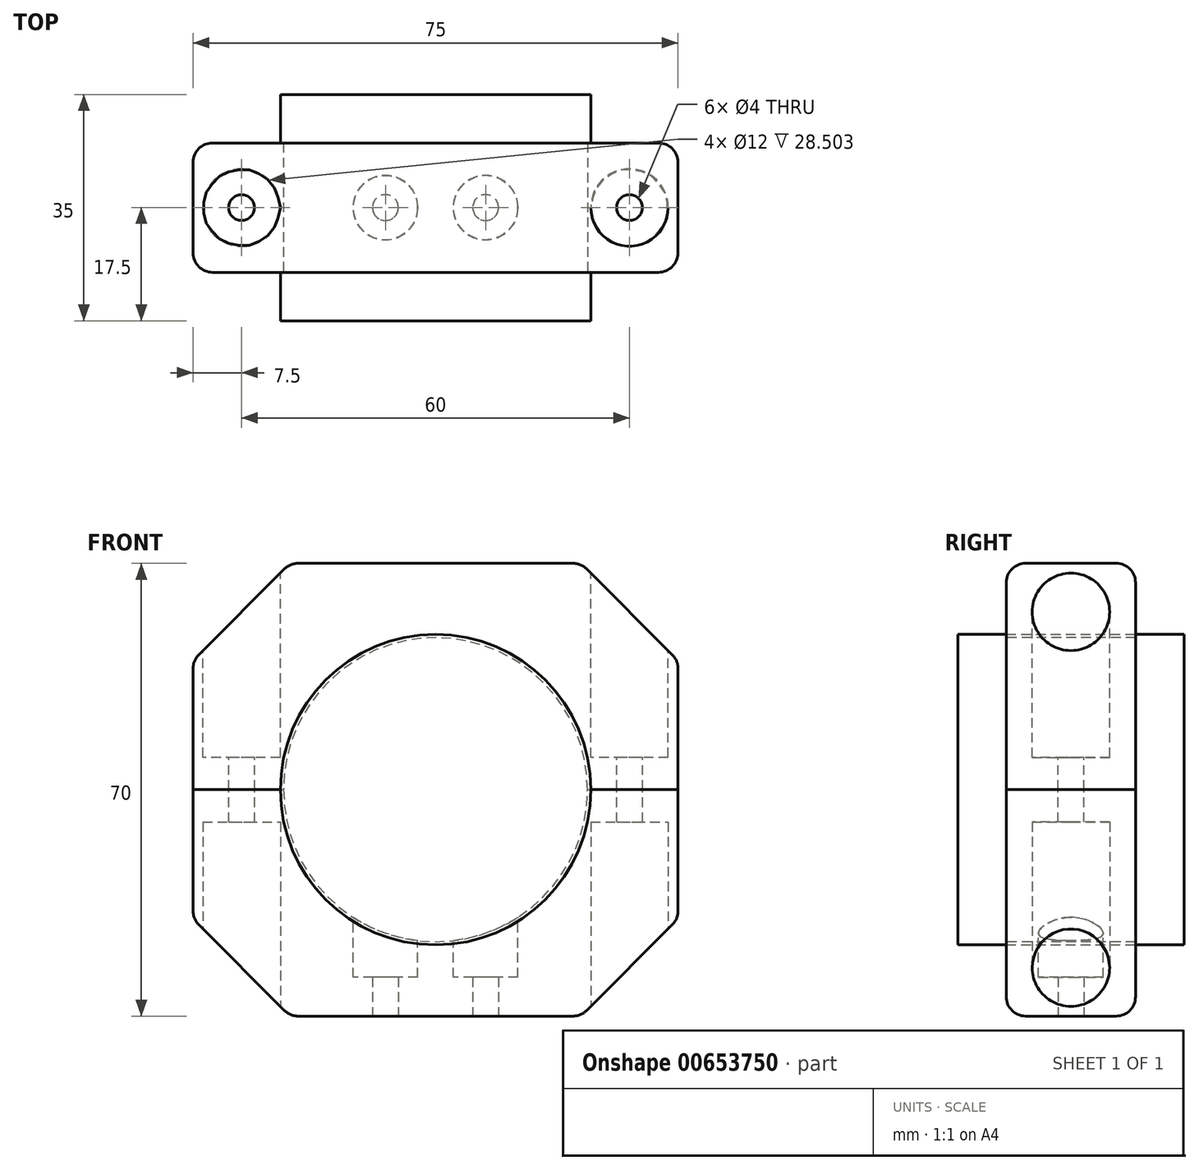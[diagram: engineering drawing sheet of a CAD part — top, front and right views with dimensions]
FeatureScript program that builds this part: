
annotation { "Feature Type Name" : "Feature", "Feature Type Description" : "" }
export const myFeature = defineFeature(function(context is Context, id is Id, definition is map)
    precondition{}
    {
        {
            var Q0;
            Q0=qCreatedBy(makeId("Top.planeOp"),FACE);
            var sketch = newSketch(context, id + "F0", { "sketchPlane" : qUnion([Q0])});
            skLineSegment(sketch, "E0.bottom", {"start": v(15, -10) * mm, "end": v(-15, -10) * mm});
            skLineSegment(sketch, "E0.top", {"start": v(15, 10) * mm, "end": v(-15, 10) * mm});
            skLineSegment(sketch, "E0.left", {"start": v(15, -10) * mm, "end": v(15, 10) * mm});
            skLineSegment(sketch, "E0.right", {"start": v(-15, -10) * mm, "end": v(-15, 10) * mm});
            skPoint(sketch, "E0.middle", {"position": v(0, 0) * mm});
            skLineSegment(sketch, "E1.bottom", {"start": v(37.5, -10) * mm, "end": v(-37.5, -10) * mm});
            skLineSegment(sketch, "E1.top", {"start": v(37.5, 10) * mm, "end": v(-37.5, 10) * mm});
            skLineSegment(sketch, "E1.left", {"start": v(37.5, -10) * mm, "end": v(37.5, 10) * mm});
            skLineSegment(sketch, "E1.right", {"start": v(-37.5, -10) * mm, "end": v(-37.5, 10) * mm});
            skSolve(sketch);
        }
        {
            var Q0;
            Q0 = qSketchRegion(id + "F0", true);
            extrude(context, id + "F1", {"entities" : qUnion([Q0]), "depth" : 35 * mm, "offsetDistance" : 25 * mm});
        }
        {
            var Q0;
            Q0=qCreatedBy(makeId("Front.planeOp"),FACE);
            var sketch = newSketch(context, id + "F2", { "sketchPlane" : qUnion([Q0])});
            skCircle(sketch, "E2", {"center": v(0, 35) * mm, "radius": 23.5 * mm});
            skSolve(sketch);
        }
        {
            var Q0;
            Q0 = qSketchRegion(id + "F2", true);
            var Q1;
            Q1=makeQuery(id+"F11.opExtrude","SWEPT_FACE",FACE,{"disambiguationData":[OSD([sQuery(id+"F10.wireOp",EDGE,"E9.bottom")])]});
            extrude(context, id + "F3", {"entities" : qUnion([Q0, Q1]), "operationType" : NewBodyOperationType.REMOVE, "endBound" : BoundingType.SYMMETRIC, "oppositeDirection" : true, "depth" : 50 * mm, "offsetDistance" : 25 * mm});
        }
        {
            var Q0;
            Q0=makeQuery(id+"F1.opExtrude","CAP_FACE",FACE,{"disambiguationData":[OSD([sQuery(id+"F0.wireOp",EDGE,"E1.bottom"),sQuery(id+"F0.wireOp",EDGE,"E1.top"),sQuery(id+"F0.wireOp",EDGE,"E1.left"),sQuery(id+"F0.wireOp",EDGE,"E1.right")])],"isStart":true});
            var sketch = newSketch(context, id + "F4", { "sketchPlane" : qUnion([Q0])});
            skCircle(sketch, "E3", {"center": v(7.75, 0) * mm, "radius": 2 * mm});
            skCircle(sketch, "E4.MirrorC", {"center": v(-7.75, 0) * mm, "radius": 2 * mm});
            skSolve(sketch);
        }
        {
            var Q0;
            Q0 = qSketchRegion(id + "F4", true);
            extrude(context, id + "F5", {"entities" : qUnion([Q0]), "operationType" : NewBodyOperationType.REMOVE, "oppositeDirection" : true, "depth" : 25 * mm, "offsetDistance" : 25 * mm});
        }
        {
            var Q0;
            {var subQ0=sQuery(id+"F0.wireOp",EDGE,"E1.bottom");var subQ1=sQuery(id+"F0.wireOp",EDGE,"E1.top");var subQ2=sQuery(id+"F0.wireOp",EDGE,"E1.left");Q0=makeQuery(id+"F3.boolean.opBoolean","SPLIT",FACE,{"disambiguationData":[TD([makeQuery(id+"F1.opExtrude","SWEPT_FACE",FACE,{"disambiguationData":[OSD([subQ2])]})])],"derivedFrom":makeQuery(id+"F1.opExtrude","CAP_FACE",FACE,{"disambiguationData":[OSD([subQ0,subQ1,subQ2,sQuery(id+"F0.wireOp",EDGE,"E1.right")])],"isStart":false})});}
            var sketch = newSketch(context, id + "F6", { "sketchPlane" : qUnion([Q0])});
            skCircle(sketch, "E5", {"center": v(7.75, 0) * mm, "radius": 5 * mm});
            skCircle(sketch, "E6.MirrorC", {"center": v(-7.75, 0) * mm, "radius": 5 * mm});
            skSolve(sketch);
        }
        {
            var Q0;
            Q0 = qSketchRegion(id + "F6", true);
            extrude(context, id + "F7", {"entities" : qUnion([Q0]), "operationType" : NewBodyOperationType.REMOVE, "oppositeDirection" : true, "depth" : 29 * mm, "offsetDistance" : 25 * mm});
        }
        {
            var Q0;
            {var subQ0=sQuery(id+"F0.wireOp",EDGE,"E1.bottom");var subQ1=sQuery(id+"F0.wireOp",EDGE,"E1.right");var subQ2=sQuery(id+"F0.wireOp",EDGE,"E1.top");Q0=makeQuery(id+"F3.boolean.opBoolean","SPLIT",FACE,{"disambiguationData":[TD([makeQuery(id+"F1.opExtrude","SWEPT_FACE",FACE,{"disambiguationData":[OSD([subQ1])]})])],"derivedFrom":makeQuery(id+"F1.opExtrude","CAP_FACE",FACE,{"disambiguationData":[OSD([subQ0,subQ2,sQuery(id+"F0.wireOp",EDGE,"E1.left"),subQ1])],"isStart":false})});}
            var sketch = newSketch(context, id + "F8", { "sketchPlane" : qUnion([Q0])});
            skCircle(sketch, "E7", {"center": v(30, 0) * mm, "radius": 2 * mm});
            skCircle(sketch, "E8.MirrorC", {"center": v(-30, 0) * mm, "radius": 2 * mm});
            skSolve(sketch);
        }
        {
            var Q0;
            Q0 = qSketchRegion(id + "F8", true);
            extrude(context, id + "F9", {"entities" : qUnion([Q0]), "operationType" : NewBodyOperationType.REMOVE, "endBound" : BoundingType.THROUGH_ALL, "oppositeDirection" : true, "depth" : 50 * mm, "offsetDistance" : 25 * mm, "hasSecondDirection" : true, "secondDirectionBound" : SecondDirectionBoundingType.THROUGH_ALL, "secondDirectionOppositeDirection" : false, "secondDirectionDepth" : 25 * mm});
        }
        {
            var Q0;
            {var subQ0=sQuery(id+"F0.wireOp",EDGE,"E1.bottom");var subQ1=sQuery(id+"F0.wireOp",EDGE,"E1.right");var subQ2=sQuery(id+"F0.wireOp",EDGE,"E1.top");Q0=makeQuery(id+"F3.boolean.opBoolean","SPLIT",FACE,{"disambiguationData":[TD([makeQuery(id+"F1.opExtrude","SWEPT_FACE",FACE,{"disambiguationData":[OSD([subQ1])]})])],"derivedFrom":makeQuery(id+"F1.opExtrude","CAP_FACE",FACE,{"disambiguationData":[OSD([subQ0,subQ2,sQuery(id+"F0.wireOp",EDGE,"E1.left"),subQ1])],"isStart":false})});}
            var sketch = newSketch(context, id + "F10", { "sketchPlane" : qUnion([Q0])});
            skLineSegment(sketch, "E9.bottom", {"start": v(-37.5, -10) * mm, "end": v(37.5, -10) * mm});
            skLineSegment(sketch, "E9.top", {"start": v(-37.5, 10) * mm, "end": v(37.5, 10) * mm});
            skLineSegment(sketch, "E9.left", {"start": v(-37.5, -10) * mm, "end": v(-37.5, 10) * mm});
            skLineSegment(sketch, "E9.right", {"start": v(37.5, -10) * mm, "end": v(37.5, 10) * mm});
            skSolve(sketch);
        }
        {
            var Q0;
            Q0 = qSketchRegion(id + "F10", true);
            extrude(context, id + "F11", {"entities" : qUnion([Q0]), "depth" : 35 * mm, "offsetDistance" : 25 * mm});
        }
        {
            var Q0;
            Q0=makeQuery(id+"F11.opExtrude","SWEPT_FACE",FACE,{"disambiguationData":[OSD([sQuery(id+"F10.wireOp",EDGE,"E9.bottom")])]});
            var sketch = newSketch(context, id + "F12", { "sketchPlane" : qUnion([Q0])});
            skCircle(sketch, "E10", {"center": v(0, 35) * mm, "radius": 23.5 * mm});
            skSolve(sketch);
        }
        {
            var Q0;
            Q0 = qSketchRegion(id + "F12", true);
            extrude(context, id + "F13", {"entities" : qUnion([Q0]), "operationType" : NewBodyOperationType.REMOVE, "endBound" : BoundingType.SYMMETRIC, "oppositeDirection" : true, "depth" : 50 * mm, "offsetDistance" : 25 * mm});
        }
        {
            var Q0;
            Q0=makeQuery(id+"F11.opExtrude","CAP_FACE",FACE,{"disambiguationData":[OSD([sQuery(id+"F10.wireOp",EDGE,"E9.bottom"),sQuery(id+"F10.wireOp",EDGE,"E9.top"),sQuery(id+"F10.wireOp",EDGE,"E9.left"),sQuery(id+"F10.wireOp",EDGE,"E9.right")])],"isStart":false});
            var sketch = newSketch(context, id + "F14", { "sketchPlane" : qUnion([Q0])});
            skCircle(sketch, "E11", {"center": v(30, 0) * mm, "radius": 2 * mm});
            skCircle(sketch, "E12.MirrorC", {"center": v(-30, 0) * mm, "radius": 2 * mm});
            skSolve(sketch);
        }
        {
            var Q0;
            Q0 = qSketchRegion(id + "F14", true);
            extrude(context, id + "F15", {"entities" : qUnion([Q0]), "operationType" : NewBodyOperationType.REMOVE, "oppositeDirection" : true, "depth" : 50 * mm, "offsetDistance" : 25 * mm});
        }
        {
            var Q0;
            Q0=makeQuery(id+"F11.opExtrude","CAP_FACE",FACE,{"disambiguationData":[OSD([sQuery(id+"F10.wireOp",EDGE,"E9.bottom"),sQuery(id+"F10.wireOp",EDGE,"E9.top"),sQuery(id+"F10.wireOp",EDGE,"E9.left"),sQuery(id+"F10.wireOp",EDGE,"E9.right")])],"isStart":false});
            var sketch = newSketch(context, id + "F16", { "sketchPlane" : qUnion([Q0])});
            skCircle(sketch, "E13", {"center": v(30, 0) * mm, "radius": 6 * mm});
            skCircle(sketch, "E14.MirrorC", {"center": v(-30, 0) * mm, "radius": 6 * mm});
            skSolve(sketch);
        }
        {
            var Q0;
            Q0 = qSketchRegion(id + "F16", true);
            extrude(context, id + "F17", {"entities" : qUnion([Q0]), "operationType" : NewBodyOperationType.REMOVE, "oppositeDirection" : true, "depth" : 30 * mm, "offsetDistance" : 25 * mm});
        }
        {
            var Q0;
            {var subQ0=sQuery(id+"F10.wireOp",EDGE,"E9.bottom");var subQ1=sQuery(id+"F10.wireOp",EDGE,"E9.right");Q0=makeQuery(id+"F17.boolean.opBoolean","SPLIT",EDGE,{"disambiguationData":[TD([makeQuery(id+"F11.opExtrude","SWEPT_FACE",FACE,{"disambiguationData":[OSD([subQ0])]})])],"derivedFrom":makeQuery(id+"F11.opExtrude","CAP_EDGE",EDGE,{"disambiguationData":[OSD([subQ1])],"isStart":false})});}
            var Q1;
            {var subQ0=sQuery(id+"F10.wireOp",EDGE,"E9.right");var subQ1=sQuery(id+"F10.wireOp",EDGE,"E9.top");Q1=makeQuery(id+"F17.boolean.opBoolean","SPLIT",EDGE,{"disambiguationData":[TD([makeQuery(id+"F11.opExtrude","SWEPT_FACE",FACE,{"disambiguationData":[OSD([subQ1])]})])],"derivedFrom":makeQuery(id+"F11.opExtrude","CAP_EDGE",EDGE,{"disambiguationData":[OSD([subQ0])],"isStart":false})});}
            var Q2;
            {var subQ0=sQuery(id+"F10.wireOp",EDGE,"E9.bottom");var subQ1=sQuery(id+"F10.wireOp",EDGE,"E9.left");Q2=makeQuery(id+"F17.boolean.opBoolean","SPLIT",EDGE,{"disambiguationData":[TD([makeQuery(id+"F11.opExtrude","SWEPT_FACE",FACE,{"disambiguationData":[OSD([subQ0])]})])],"derivedFrom":makeQuery(id+"F11.opExtrude","CAP_EDGE",EDGE,{"disambiguationData":[OSD([subQ1])],"isStart":false})});}
            var Q3;
            {var subQ0=sQuery(id+"F10.wireOp",EDGE,"E9.left");var subQ1=sQuery(id+"F10.wireOp",EDGE,"E9.top");Q3=makeQuery(id+"F17.boolean.opBoolean","SPLIT",EDGE,{"disambiguationData":[TD([makeQuery(id+"F11.opExtrude","SWEPT_FACE",FACE,{"disambiguationData":[OSD([subQ1])]})])],"derivedFrom":makeQuery(id+"F11.opExtrude","CAP_EDGE",EDGE,{"disambiguationData":[OSD([subQ0])],"isStart":false})});}
            chamfer(context, id + "F18", {"entities" : qUnion([Q0, Q1, Q2, Q3]), "width" : 15 * mm, "tangentPropagation" : true});
        }
        {
            var Q0;
            Q0=makeQuery(id+"F1.opExtrude","CAP_EDGE",EDGE,{"disambiguationData":[OSD([sQuery(id+"F0.wireOp",EDGE,"E1.left")])],"isStart":true});
            var Q1;
            Q1=makeQuery(id+"F1.opExtrude","CAP_EDGE",EDGE,{"disambiguationData":[OSD([sQuery(id+"F0.wireOp",EDGE,"E1.right")])],"isStart":true});
            chamfer(context, id + "F19", {"entities" : qUnion([Q0, Q1]), "width" : 15 * mm, "tangentPropagation" : true});
        }
        {
            var Q0;
            Q0=qCreatedBy(makeId("Front.planeOp"),FACE);
            var sketch = newSketch(context, id + "F20", { "sketchPlane" : qUnion([Q0])});
            skCircle(sketch, "E15", {"center": v(0, 35) * mm, "radius": 24 * mm});
            skSolve(sketch);
        }
        {
            var Q0;
            Q0 = qSketchRegion(id + "F20", true);
            extrude(context, id + "F21", {"entities" : qUnion([Q0]), "endBound" : BoundingType.SYMMETRIC, "depth" : 35 * mm, "offsetDistance" : 25 * mm});
        }
        {
            var Q0;
            {var subQ0=sQuery(id+"F10.wireOp",EDGE,"E9.right");var subQ1=sQuery(id+"F10.wireOp",EDGE,"E9.bottom");var subQ2=makeQuery(id+"F11.opExtrude","CAP_FACE",FACE,{"disambiguationData":[OSD([subQ1,sQuery(id+"F10.wireOp",EDGE,"E9.top"),sQuery(id+"F10.wireOp",EDGE,"E9.left"),subQ0])],"isStart":false});Q0=makeQuery(id+"F18.opChamfer","BLEND_EDGE",EDGE,{"blendedFrom":[makeQuery(id+"F17.boolean.opBoolean","SPLIT",EDGE,{"disambiguationData":[TD([makeQuery(id+"F11.opExtrude","SWEPT_FACE",FACE,{"disambiguationData":[OSD([subQ1])]})])],"derivedFrom":makeQuery(id+"F11.opExtrude","CAP_EDGE",EDGE,{"disambiguationData":[OSD([subQ0])],"isStart":false})}),subQ2],"blendedInto":[subQ2]});}
            var Q1;
            {var subQ0=sQuery(id+"F10.wireOp",EDGE,"E9.right");var subQ1=makeQuery(id+"F11.opExtrude","SWEPT_FACE",FACE,{"disambiguationData":[OSD([subQ0])]});var subQ2=sQuery(id+"F10.wireOp",EDGE,"E9.bottom");Q1=makeQuery(id+"F18.opChamfer","BLEND_EDGE",EDGE,{"disambiguationData":[OD(0.0)],"blendedFrom":[makeQuery(id+"F17.boolean.opBoolean","SPLIT",EDGE,{"disambiguationData":[TD([makeQuery(id+"F11.opExtrude","SWEPT_FACE",FACE,{"disambiguationData":[OSD([subQ2])]})])],"derivedFrom":makeQuery(id+"F11.opExtrude","CAP_EDGE",EDGE,{"disambiguationData":[OSD([subQ0])],"isStart":false})}),subQ1],"blendedInto":[subQ1]});}
            var Q2;
            {var subQ0=sQuery(id+"F10.wireOp",EDGE,"E9.right");var subQ1=makeQuery(id+"F11.opExtrude","SWEPT_FACE",FACE,{"disambiguationData":[OSD([subQ0])]});var subQ2=sQuery(id+"F10.wireOp",EDGE,"E9.bottom");Q2=makeQuery(id+"F18.opChamfer","BLEND_EDGE",EDGE,{"disambiguationData":[OD(1.0)],"blendedFrom":[makeQuery(id+"F17.boolean.opBoolean","SPLIT",EDGE,{"disambiguationData":[TD([makeQuery(id+"F11.opExtrude","SWEPT_FACE",FACE,{"disambiguationData":[OSD([subQ2])]})])],"derivedFrom":makeQuery(id+"F11.opExtrude","CAP_EDGE",EDGE,{"disambiguationData":[OSD([subQ0])],"isStart":false})}),subQ1],"blendedInto":[subQ1]});}
            var Q3;
            Q3=makeQuery(id+"F11.opExtrude","CAP_EDGE",EDGE,{"disambiguationData":[OSD([sQuery(id+"F10.wireOp",EDGE,"E9.bottom")])],"isStart":false});
            var Q4;
            {var subQ0=sQuery(id+"F10.wireOp",EDGE,"E9.bottom");var subQ1=makeQuery(id+"F11.opExtrude","SWEPT_FACE",FACE,{"disambiguationData":[OSD([subQ0])]});var subQ2=sQuery(id+"F10.wireOp",EDGE,"E9.right");Q4=makeQuery(id+"F18.opChamfer","BLEND_EDGE",EDGE,{"blendedFrom":[makeQuery(id+"F17.boolean.opBoolean","SPLIT",EDGE,{"disambiguationData":[TD([subQ1])],"derivedFrom":makeQuery(id+"F11.opExtrude","CAP_EDGE",EDGE,{"disambiguationData":[OSD([subQ2])],"isStart":false})}),subQ1],"blendedInto":[subQ1]});}
            var Q5;
            Q5=makeQuery(id+"F11.opExtrude","SWEPT_EDGE",EDGE,{"disambiguationData":[OSD([sQuery(id+"F10.wireOp",EDGE,"E9.bottom"),sQuery(id+"F10.wireOp",EDGE,"E9.right")])]});
            var Q6;
            Q6=makeQuery(id+"F1.opExtrude","SWEPT_EDGE",EDGE,{"disambiguationData":[OSD([sQuery(id+"F0.wireOp",EDGE,"E1.bottom"),sQuery(id+"F0.wireOp",EDGE,"E1.left")])]});
            var Q7;
            Q7=makeQuery(id+"F19.opChamfer","BLEND_EDGE",EDGE,{"blendedFrom":[makeQuery(id+"F1.opExtrude","CAP_EDGE",EDGE,{"disambiguationData":[OSD([sQuery(id+"F0.wireOp",EDGE,"E1.left")])],"isStart":true}),makeQuery(id+"F1.opExtrude","SWEPT_FACE",FACE,{"disambiguationData":[OSD([sQuery(id+"F0.wireOp",EDGE,"E1.bottom")])]})],"blendedInto":[makeQuery(id+"F1.opExtrude","SWEPT_FACE",FACE,{"disambiguationData":[OSD([sQuery(id+"F0.wireOp",EDGE,"E1.bottom")])]})]});
            var Q8;
            {var subQ0=sQuery(id+"F0.wireOp",EDGE,"E1.left");Q8=makeQuery(id+"F19.opChamfer","BLEND_EDGE",EDGE,{"blendedFrom":[makeQuery(id+"F1.opExtrude","CAP_EDGE",EDGE,{"disambiguationData":[OSD([subQ0])],"isStart":true}),makeQuery(id+"F1.opExtrude","SWEPT_FACE",FACE,{"disambiguationData":[OSD([subQ0])]})],"blendedInto":[makeQuery(id+"F1.opExtrude","SWEPT_FACE",FACE,{"disambiguationData":[OSD([subQ0])]})]});}
            var Q9;
            {var subQ0=sQuery(id+"F10.wireOp",EDGE,"E9.bottom");var subQ1=makeQuery(id+"F11.opExtrude","SWEPT_FACE",FACE,{"disambiguationData":[OSD([subQ0])]});var subQ2=sQuery(id+"F10.wireOp",EDGE,"E9.left");Q9=makeQuery(id+"F18.opChamfer","BLEND_EDGE",EDGE,{"blendedFrom":[makeQuery(id+"F17.boolean.opBoolean","SPLIT",EDGE,{"disambiguationData":[TD([subQ1])],"derivedFrom":makeQuery(id+"F11.opExtrude","CAP_EDGE",EDGE,{"disambiguationData":[OSD([subQ2])],"isStart":false})}),subQ1],"blendedInto":[subQ1]});}
            var Q10;
            Q10=makeQuery(id+"F11.opExtrude","SWEPT_EDGE",EDGE,{"disambiguationData":[OSD([sQuery(id+"F10.wireOp",EDGE,"E9.bottom"),sQuery(id+"F10.wireOp",EDGE,"E9.left")])]});
            var Q11;
            Q11=makeQuery(id+"F1.opExtrude","SWEPT_EDGE",EDGE,{"disambiguationData":[OSD([sQuery(id+"F0.wireOp",EDGE,"E1.bottom"),sQuery(id+"F0.wireOp",EDGE,"E1.right")])]});
            var Q12;
            Q12=makeQuery(id+"F19.opChamfer","BLEND_EDGE",EDGE,{"blendedFrom":[makeQuery(id+"F1.opExtrude","CAP_EDGE",EDGE,{"disambiguationData":[OSD([sQuery(id+"F0.wireOp",EDGE,"E1.right")])],"isStart":true}),makeQuery(id+"F1.opExtrude","SWEPT_FACE",FACE,{"disambiguationData":[OSD([sQuery(id+"F0.wireOp",EDGE,"E1.bottom")])]})],"blendedInto":[makeQuery(id+"F1.opExtrude","SWEPT_FACE",FACE,{"disambiguationData":[OSD([sQuery(id+"F0.wireOp",EDGE,"E1.bottom")])]})]});
            var Q13;
            {var subQ0=sQuery(id+"F10.wireOp",EDGE,"E9.top");var subQ1=sQuery(id+"F10.wireOp",EDGE,"E9.bottom");var subQ2=sQuery(id+"F10.wireOp",EDGE,"E9.right");Q13=makeQuery(id+"F18.opChamfer","BLEND_EDGE",EDGE,{"blendedFrom":[makeQuery(id+"F17.boolean.opBoolean","SPLIT",EDGE,{"disambiguationData":[TD([makeQuery(id+"F11.opExtrude","SWEPT_FACE",FACE,{"disambiguationData":[OSD([subQ1])]})])],"derivedFrom":makeQuery(id+"F11.opExtrude","CAP_EDGE",EDGE,{"disambiguationData":[OSD([subQ2])],"isStart":false})}),makeQuery(id+"F11.opExtrude","SWEPT_FACE",FACE,{"disambiguationData":[OSD([subQ0])]})],"blendedInto":[makeQuery(id+"F11.opExtrude","SWEPT_FACE",FACE,{"disambiguationData":[OSD([subQ0])]})]});}
            var Q14;
            Q14=makeQuery(id+"F11.opExtrude","CAP_EDGE",EDGE,{"disambiguationData":[OSD([sQuery(id+"F10.wireOp",EDGE,"E9.top")])],"isStart":false});
            var Q15;
            {var subQ0=sQuery(id+"F10.wireOp",EDGE,"E9.top");var subQ1=sQuery(id+"F10.wireOp",EDGE,"E9.bottom");var subQ2=sQuery(id+"F10.wireOp",EDGE,"E9.left");Q15=makeQuery(id+"F18.opChamfer","BLEND_EDGE",EDGE,{"blendedFrom":[makeQuery(id+"F17.boolean.opBoolean","SPLIT",EDGE,{"disambiguationData":[TD([makeQuery(id+"F11.opExtrude","SWEPT_FACE",FACE,{"disambiguationData":[OSD([subQ1])]})])],"derivedFrom":makeQuery(id+"F11.opExtrude","CAP_EDGE",EDGE,{"disambiguationData":[OSD([subQ2])],"isStart":false})}),makeQuery(id+"F11.opExtrude","SWEPT_FACE",FACE,{"disambiguationData":[OSD([subQ0])]})],"blendedInto":[makeQuery(id+"F11.opExtrude","SWEPT_FACE",FACE,{"disambiguationData":[OSD([subQ0])]})]});}
            var Q16;
            Q16=makeQuery(id+"F11.opExtrude","SWEPT_EDGE",EDGE,{"disambiguationData":[OSD([sQuery(id+"F10.wireOp",EDGE,"E9.top"),sQuery(id+"F10.wireOp",EDGE,"E9.left")])]});
            var Q17;
            Q17=makeQuery(id+"F1.opExtrude","SWEPT_EDGE",EDGE,{"disambiguationData":[OSD([sQuery(id+"F0.wireOp",EDGE,"E1.top"),sQuery(id+"F0.wireOp",EDGE,"E1.right")])]});
            var Q18;
            Q18=makeQuery(id+"F19.opChamfer","BLEND_EDGE",EDGE,{"blendedFrom":[makeQuery(id+"F1.opExtrude","CAP_EDGE",EDGE,{"disambiguationData":[OSD([sQuery(id+"F0.wireOp",EDGE,"E1.right")])],"isStart":true}),makeQuery(id+"F1.opExtrude","SWEPT_FACE",FACE,{"disambiguationData":[OSD([sQuery(id+"F0.wireOp",EDGE,"E1.top")])]})],"blendedInto":[makeQuery(id+"F1.opExtrude","SWEPT_FACE",FACE,{"disambiguationData":[OSD([sQuery(id+"F0.wireOp",EDGE,"E1.top")])]})]});
            var Q19;
            Q19=makeQuery(id+"F19.opChamfer","BLEND_EDGE",EDGE,{"blendedFrom":[makeQuery(id+"F1.opExtrude","CAP_EDGE",EDGE,{"disambiguationData":[OSD([sQuery(id+"F0.wireOp",EDGE,"E1.left")])],"isStart":true}),makeQuery(id+"F1.opExtrude","SWEPT_FACE",FACE,{"disambiguationData":[OSD([sQuery(id+"F0.wireOp",EDGE,"E1.top")])]})],"blendedInto":[makeQuery(id+"F1.opExtrude","SWEPT_FACE",FACE,{"disambiguationData":[OSD([sQuery(id+"F0.wireOp",EDGE,"E1.top")])]})]});
            var Q20;
            Q20=makeQuery(id+"F11.opExtrude","SWEPT_EDGE",EDGE,{"disambiguationData":[OSD([sQuery(id+"F10.wireOp",EDGE,"E9.top"),sQuery(id+"F10.wireOp",EDGE,"E9.right")])]});
            var Q21;
            Q21=makeQuery(id+"F1.opExtrude","SWEPT_EDGE",EDGE,{"disambiguationData":[OSD([sQuery(id+"F0.wireOp",EDGE,"E1.top"),sQuery(id+"F0.wireOp",EDGE,"E1.left")])]});
            var Q22;
            {var subQ0=sQuery(id+"F10.wireOp",EDGE,"E9.left");var subQ1=makeQuery(id+"F11.opExtrude","SWEPT_FACE",FACE,{"disambiguationData":[OSD([subQ0])]});var subQ2=sQuery(id+"F10.wireOp",EDGE,"E9.bottom");Q22=makeQuery(id+"F18.opChamfer","BLEND_EDGE",EDGE,{"disambiguationData":[OD(1.0)],"blendedFrom":[makeQuery(id+"F17.boolean.opBoolean","SPLIT",EDGE,{"disambiguationData":[TD([makeQuery(id+"F11.opExtrude","SWEPT_FACE",FACE,{"disambiguationData":[OSD([subQ2])]})])],"derivedFrom":makeQuery(id+"F11.opExtrude","CAP_EDGE",EDGE,{"disambiguationData":[OSD([subQ0])],"isStart":false})}),subQ1],"blendedInto":[subQ1]});}
            var Q23;
            {var subQ0=sQuery(id+"F10.wireOp",EDGE,"E9.left");var subQ1=makeQuery(id+"F11.opExtrude","SWEPT_FACE",FACE,{"disambiguationData":[OSD([subQ0])]});var subQ2=sQuery(id+"F10.wireOp",EDGE,"E9.bottom");Q23=makeQuery(id+"F18.opChamfer","BLEND_EDGE",EDGE,{"disambiguationData":[OD(0.0)],"blendedFrom":[makeQuery(id+"F17.boolean.opBoolean","SPLIT",EDGE,{"disambiguationData":[TD([makeQuery(id+"F11.opExtrude","SWEPT_FACE",FACE,{"disambiguationData":[OSD([subQ2])]})])],"derivedFrom":makeQuery(id+"F11.opExtrude","CAP_EDGE",EDGE,{"disambiguationData":[OSD([subQ0])],"isStart":false})}),subQ1],"blendedInto":[subQ1]});}
            var Q24;
            {var subQ0=sQuery(id+"F10.wireOp",EDGE,"E9.left");var subQ1=sQuery(id+"F10.wireOp",EDGE,"E9.bottom");var subQ2=makeQuery(id+"F11.opExtrude","CAP_FACE",FACE,{"disambiguationData":[OSD([subQ1,sQuery(id+"F10.wireOp",EDGE,"E9.top"),subQ0,sQuery(id+"F10.wireOp",EDGE,"E9.right")])],"isStart":false});Q24=makeQuery(id+"F18.opChamfer","BLEND_EDGE",EDGE,{"blendedFrom":[makeQuery(id+"F17.boolean.opBoolean","SPLIT",EDGE,{"disambiguationData":[TD([makeQuery(id+"F11.opExtrude","SWEPT_FACE",FACE,{"disambiguationData":[OSD([subQ1])]})])],"derivedFrom":makeQuery(id+"F11.opExtrude","CAP_EDGE",EDGE,{"disambiguationData":[OSD([subQ0])],"isStart":false})}),subQ2],"blendedInto":[subQ2]});}
            var Q25;
            {var subQ0=sQuery(id+"F0.wireOp",EDGE,"E1.right");Q25=makeQuery(id+"F19.opChamfer","BLEND_EDGE",EDGE,{"blendedFrom":[makeQuery(id+"F1.opExtrude","CAP_EDGE",EDGE,{"disambiguationData":[OSD([subQ0])],"isStart":true}),makeQuery(id+"F1.opExtrude","SWEPT_FACE",FACE,{"disambiguationData":[OSD([subQ0])]})],"blendedInto":[makeQuery(id+"F1.opExtrude","SWEPT_FACE",FACE,{"disambiguationData":[OSD([subQ0])]})]});}
            var Q26;
            Q26=makeQuery(id+"F1.opExtrude","CAP_EDGE",EDGE,{"disambiguationData":[OSD([sQuery(id+"F0.wireOp",EDGE,"E1.bottom")])],"isStart":true});
            var Q27;
            Q27=makeQuery(id+"F1.opExtrude","CAP_EDGE",EDGE,{"disambiguationData":[OSD([sQuery(id+"F0.wireOp",EDGE,"E1.top")])],"isStart":true});
            var Q28;
            {var subQ0=sQuery(id+"F0.wireOp",EDGE,"E1.left");Q28=makeQuery(id+"F19.opChamfer","BLEND_EDGE",EDGE,{"blendedFrom":[makeQuery(id+"F1.opExtrude","CAP_EDGE",EDGE,{"disambiguationData":[OSD([subQ0])],"isStart":true}),makeQuery(id+"F1.opExtrude","CAP_FACE",FACE,{"disambiguationData":[OSD([sQuery(id+"F0.wireOp",EDGE,"E1.bottom"),sQuery(id+"F0.wireOp",EDGE,"E1.top"),subQ0,sQuery(id+"F0.wireOp",EDGE,"E1.right")])],"isStart":true})],"blendedInto":[makeQuery(id+"F1.opExtrude","CAP_FACE",FACE,{"disambiguationData":[OSD([sQuery(id+"F0.wireOp",EDGE,"E1.bottom"),sQuery(id+"F0.wireOp",EDGE,"E1.top"),subQ0,sQuery(id+"F0.wireOp",EDGE,"E1.right")])],"isStart":true})]});}
            var Q29;
            {var subQ0=sQuery(id+"F0.wireOp",EDGE,"E1.right");Q29=makeQuery(id+"F19.opChamfer","BLEND_EDGE",EDGE,{"blendedFrom":[makeQuery(id+"F1.opExtrude","CAP_EDGE",EDGE,{"disambiguationData":[OSD([subQ0])],"isStart":true}),makeQuery(id+"F1.opExtrude","CAP_FACE",FACE,{"disambiguationData":[OSD([sQuery(id+"F0.wireOp",EDGE,"E1.bottom"),sQuery(id+"F0.wireOp",EDGE,"E1.top"),sQuery(id+"F0.wireOp",EDGE,"E1.left"),subQ0])],"isStart":true})],"blendedInto":[makeQuery(id+"F1.opExtrude","CAP_FACE",FACE,{"disambiguationData":[OSD([sQuery(id+"F0.wireOp",EDGE,"E1.bottom"),sQuery(id+"F0.wireOp",EDGE,"E1.top"),sQuery(id+"F0.wireOp",EDGE,"E1.left"),subQ0])],"isStart":true})]});}
            fillet(context, id + "F22", {"entities" : qUnion([Q0, Q1, Q2, Q3, Q4, Q5, Q6, Q7, Q8, Q9, Q10, Q11, Q12, Q13, Q14, Q15, Q16, Q17, Q18, Q19, Q20, Q21, Q22, Q23, Q24, Q25, Q26, Q27, Q28, Q29]), "radius" : 3 * mm, "tangentPropagation" : true, "allowEdgeOverflow" : false});
        }
        {
            var Q0;
            Q0=makeQuery(id+"F1.opExtrude","CAP_FACE",FACE,{"disambiguationData":[OSD([sQuery(id+"F0.wireOp",EDGE,"E1.bottom"),sQuery(id+"F0.wireOp",EDGE,"E1.top"),sQuery(id+"F0.wireOp",EDGE,"E1.left"),sQuery(id+"F0.wireOp",EDGE,"E1.right")])],"isStart":true});
            var sketch = newSketch(context, id + "F23", { "sketchPlane" : qUnion([Q0])});
            skCircle(sketch, "E16", {"center": v(30, 0) * mm, "radius": 6 * mm});
            skCircle(sketch, "E17.MirrorC", {"center": v(-30, 0) * mm, "radius": 6 * mm});
            skSolve(sketch);
        }
        {
            var Q0;
            Q0 = qSketchRegion(id + "F23", true);
            extrude(context, id + "F24", {"entities" : qUnion([Q0]), "operationType" : NewBodyOperationType.REMOVE, "oppositeDirection" : true, "depth" : 30 * mm, "offsetDistance" : 25 * mm});
        }
    });
